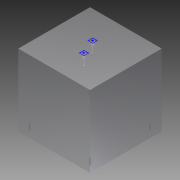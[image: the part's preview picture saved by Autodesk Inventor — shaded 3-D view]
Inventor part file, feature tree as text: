
AUTODESK INVENTOR PART (.ipt)
format: ipt  version: 2014 (Build 180170000, 170)  size: 291,328 bytes
history: native  units: mm
features: other x51, sketch x4, extrude x1
ambient origin geometry x8: Origin, YZ Plane, XZ Plane, XY Plane, X Axis, Y Axis, Z Axis, Center Point
bodies: 实体1 (feature_tree)
feature tree (56):
  extrude  "拉伸1"  TaperAngle=0.0deg  [1 undecoded]
  other  "UCS1"
  other  "UCS2"
  other  "UCS3"
  other  "UCS4"
  other  "UCS5"
  other  "UCS6"
  other  "Footprint7"
  other  "Footprint2"
  other  "iFeature2:2"
  sketch  "草图1"  dims[d0=1000.0mm d1=0.0mm]
  other  "UCS1: YZ 平面"
  other  "UCS1: XZ 平面"
  other  "UCS1: XY 平面"
  other  "UCS1: X 轴"
  other  "UCS1: Y 轴"
  other  "UCS1: Z 轴"
  other  "UCS1: 原点"
  other  "UCS2: YZ 平面"
  other  "UCS2: XZ 平面"
  other  "UCS2: XY 平面"
  other  "UCS2: X 轴"
  other  "UCS2: Y 轴"
  other  "UCS2: Z 轴"
  other  "UCS2: 原点"
  other  "UCS3: YZ 平面"
  other  "UCS3: XZ 平面"
  other  "UCS3: XY 平面"
  other  "UCS3: X 轴"
  other  "UCS3: Y 轴"
  other  "UCS3: Z 轴"
  other  "UCS3: 原点"
  other  "UCS4: YZ 平面"
  other  "UCS4: XZ 平面"
  other  "UCS4: XY 平面"
  other  "UCS4: X 轴"
  other  "UCS4: Y 轴"
  other  "UCS4: Z 轴"
  other  "UCS4: 原点"
  other  "UCS5: YZ 平面"
  other  "UCS5: XZ 平面"
  other  "UCS5: XY 平面"
  other  "UCS5: X 轴"
  other  "UCS5: Y 轴"
  other  "UCS5: Z 轴"
  other  "UCS5: 原点"
  other  "UCS6: YZ 平面"
  other  "UCS6: XZ 平面"
  other  "UCS6: XY 平面"
  other  "UCS6: X 轴"
  other  "UCS6: Y 轴"
  other  "UCS6: Z 轴"
  other  "UCS6: 原点"
  sketch  "草图15"  dims[d2=0.0mm d3=0.0mm d4=0.0mm d5=0.0mm d6=0.0mm d7=0.0mm]
  sketch  "草图17"  dims[d8=0.0mm d9=0.0mm d10=0.0mm d11=0.0mm d12=0.0mm d13=0.0mm]
  sketch  "草图20"  dims[d14=0.0mm d15=0.0mm d16=0.0mm d17=0.0mm d18=0.0mm d19=0.0mm d20=0.0mm d21=0.0mm d22=0.0mm d23=0.0mm d24=0.0mm d25=0.0mm d26=0.0mm d27=0.0mm d28=0.0mm d29=0.0mm d30=0.0mm d31=0.0mm d32=0.0mm d33=0.0mm d34=0.0mm d35=0.0mm d36=0.0mm d37=0.0mm d38=0.0mm d44=0.0mm d48=0.0mm d54=0.0mm d60=0.0mm d66=0.0mm d72=0.0mm d73=0.0mm d84=0.0mm]
note: 1 required parameter value undecoded (feature->parameter linkage not recoverable at this tier; creation-order binding heuristic only, values carry confidence <= 0.55)
